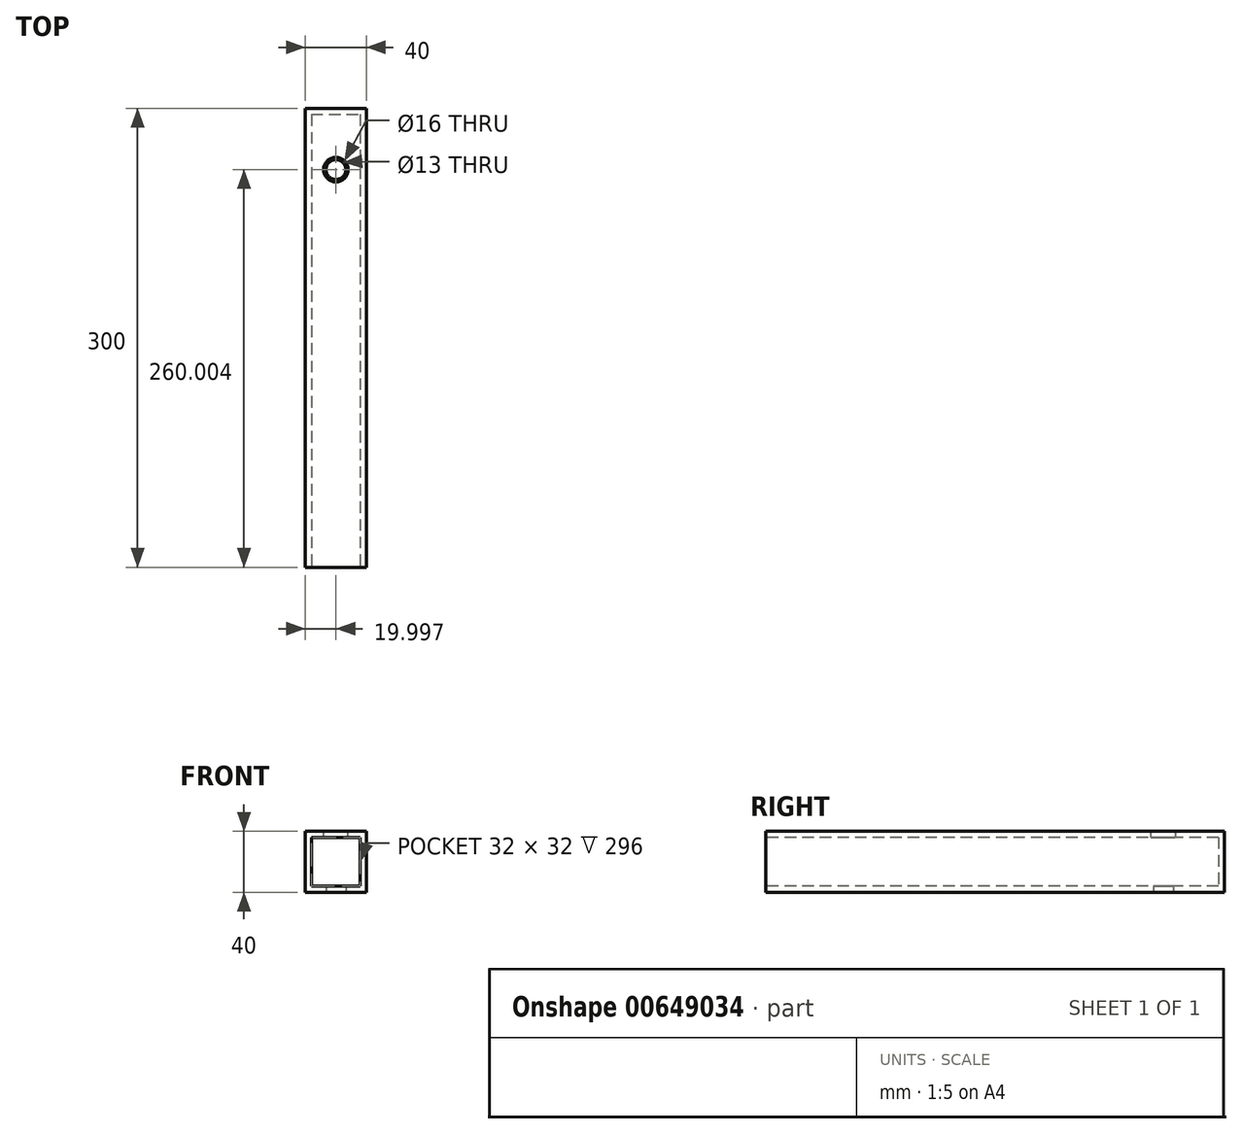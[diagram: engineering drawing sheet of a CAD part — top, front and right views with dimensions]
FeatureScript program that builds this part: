
annotation { "Feature Type Name" : "Feature", "Feature Type Description" : "" }
export const myFeature = defineFeature(function(context is Context, id is Id, definition is map)
    precondition{}
    {
        {
            var Q0;
            Q0=qCreatedBy(makeId("Top.planeOp"),FACE);
            var sketch = newSketch(context, id + "F0", { "sketchPlane" : qUnion([Q0])});
            skLineSegment(sketch, "E0.bottom", {"start": v(-23.1, 265.2) * mm, "end": v(16.9, 265.2) * mm});
            skLineSegment(sketch, "E0.top", {"start": v(-23.1, -34.8) * mm, "end": v(16.9, -34.8) * mm});
            skLineSegment(sketch, "E0.left", {"start": v(-23.1, 265.2) * mm, "end": v(-23.1, -34.8) * mm});
            skLineSegment(sketch, "E0.right", {"start": v(16.9, 265.2) * mm, "end": v(16.9, -34.8) * mm});
            skSolve(sketch);
        }
        {
            var Q0;
            Q0=makeQuery(id+"F0.imprint","IMPRINT",FACE,{"disambiguationData":[TD([[makeQuery(id+"F0.imprint","IMPRINT",EDGE,{"derivedFrom":sQuery(id+"F0.wireOp",EDGE,"E0.bottom")}),-1.0]])]});
            extrude(context, id + "F1", {"entities" : qUnion([Q0]), "depth" : 40 * mm, "offsetDistance" : 25 * mm});
        }
        {
            var Q0;
            Q0=makeQuery(id+"F1.opExtrude","SWEPT_FACE",FACE,{"disambiguationData":[OSD([sQuery(id+"F0.wireOp",EDGE,"E0.top")])]});
            shell(context, id + "F2", {"entities" : qUnion([Q0]), "thickness" : 4 * mm});
        }
        {
            var Q0;
            Q0=makeQuery(id+"F1.opExtrude","CAP_FACE",FACE,{"disambiguationData":[OSD([sQuery(id+"F0.wireOp",EDGE,"E0.bottom"),sQuery(id+"F0.wireOp",EDGE,"E0.top"),sQuery(id+"F0.wireOp",EDGE,"E0.left"),sQuery(id+"F0.wireOp",EDGE,"E0.right")])],"isStart":false});
            var sketch = newSketch(context, id + "F3", { "sketchPlane" : qUnion([Q0])});
            skCircle(sketch, "E1", {"center": v(-3.1, 225.2) * mm, "radius": 8 * mm});
            skSolve(sketch);
        }
        {
            var Q0;
            Q0=sQuery(id+"F3.wireOp",VERTEX,"E1.center");
            var Q1;
            Q1=makeQuery(id+"F1.opExtrude","SWEPT_BODY",BODY,{"disambiguationData":[OSD([sQuery(id+"F0.wireOp",EDGE,"E0.bottom"),sQuery(id+"F0.wireOp",EDGE,"E0.top"),sQuery(id+"F0.wireOp",EDGE,"E0.left"),sQuery(id+"F0.wireOp",EDGE,"E0.right")])]});
            hole(context, id + "F4", {"style" : HoleStyle.SIMPLE, "endStyle" : HoleEndStyle.BLIND, "holeDiameter" : 16 * mm, "majorDiameter" : 5 * mm, "holeDepth" : 4 * mm, "isTappedThrough" : true, "tappedDepth" : 12 * mm, "tapClearance" : 3, "locations" : qUnion([Q0]), "scope" : qUnion([Q1])});
        }
        {
            var Q0;
            Q0=makeQuery(id+"F1.opExtrude","CAP_FACE",FACE,{"disambiguationData":[OSD([sQuery(id+"F0.wireOp",EDGE,"E0.bottom"),sQuery(id+"F0.wireOp",EDGE,"E0.top"),sQuery(id+"F0.wireOp",EDGE,"E0.left"),sQuery(id+"F0.wireOp",EDGE,"E0.right")])],"isStart":true});
            var sketch = newSketch(context, id + "F5", { "sketchPlane" : qUnion([Q0])});
            skCircle(sketch, "E2", {"center": v(-3.1, -225.2) * mm, "radius": 6.5 * mm});
            skSolve(sketch);
        }
        {
            var Q0;
            Q0=sQuery(id+"F5.wireOp",VERTEX,"E2.center");
            var Q1;
            Q1=makeQuery(id+"F1.opExtrude","SWEPT_BODY",BODY,{"disambiguationData":[OSD([sQuery(id+"F0.wireOp",EDGE,"E0.bottom"),sQuery(id+"F0.wireOp",EDGE,"E0.top"),sQuery(id+"F0.wireOp",EDGE,"E0.left"),sQuery(id+"F0.wireOp",EDGE,"E0.right")])]});
            hole(context, id + "F6", {"style" : HoleStyle.SIMPLE, "endStyle" : HoleEndStyle.BLIND, "holeDiameter" : 13 * mm, "majorDiameter" : 5 * mm, "holeDepth" : 4 * mm, "isTappedThrough" : true, "tappedDepth" : 12 * mm, "tapClearance" : 3, "locations" : qUnion([Q0]), "scope" : qUnion([Q1])});
        }
    });
